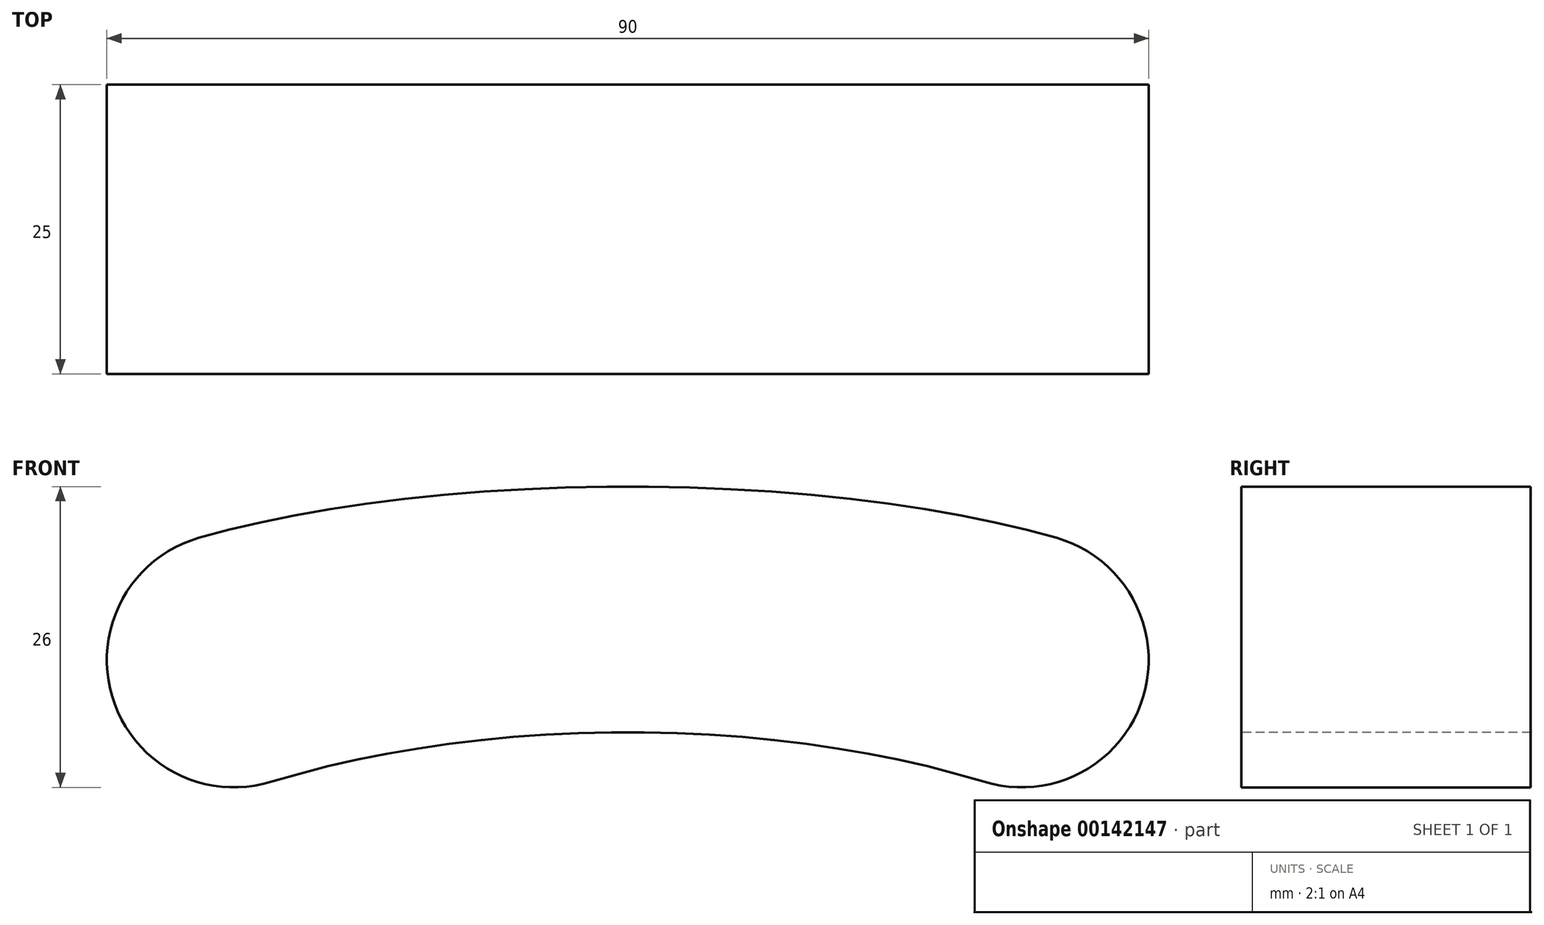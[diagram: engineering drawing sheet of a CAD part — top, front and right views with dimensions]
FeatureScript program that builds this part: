
annotation { "Feature Type Name" : "Feature", "Feature Type Description" : "" }
export const myFeature = defineFeature(function(context is Context, id is Id, definition is map)
    precondition{}
    {
        {
            var Q0;
            Q0=qCreatedBy(makeId("Front.planeOp"),FACE);
            var sketch = newSketch(context, id + "F0", { "sketchPlane" : qUnion([Q0])});
            skEllipticalArc(sketch, "E0", {});
            skArc(sketch, "E1", {"start": v(-37.06, 10.57) * mm, "mid": v(-44.54, -3.14) * mm, "end": v(-30.77, -10.52) * mm});
            skLineSegment(sketch, "E2", {"start": v(0, 0) * mm, "end": v(0, 37.33) * mm});
            skArc(sketch, "E3.MirrorC", {"start": v(37.06, 10.57) * mm, "mid": v(44.54, -3.14) * mm, "end": v(30.77, -10.52) * mm});
            skEllipticalArc(sketch, "E4", {});
            const initialGuessF0  = {"E0": [0, 0, -1, 0, 0.05221074160037808, 0.015, 3.9231845518510733, 5.501593408918306], "E4": [0, -0.031236615566046604, -1, 0, 0.055, 0.025, 4.118592204862835, 5.306185755906545]};
            skSetInitialGuess(sketch, initialGuessF0);
            skSolve(sketch);
        }
        {
            var Q0;
            Q0 = qSketchRegion(id + "F0", true);
            extrude(context, id + "F1", {"entities" : qUnion([Q0]), "endBound" : BoundingType.SYMMETRIC, "depth" : 25 * mm});
        }
    });
